# Revit family: Faucet-Brizo-Tresa-Single Handle Vessel Lavatory Faucet-65436LF
name_source: partatom
category: Plumbing Fixtures
units: mm (PartAtom-declared; Revit-internal decimal feet)

## family parameters
Always vertical = Yes
Cut with Voids When Loaded = No
OmniClass Number = 23.45.00.00
OmniClass Title = Sanitary, Laundry, and Cleaning Equipment
Part Type = Normal
Room Calculation Point = No
Round Connector Dimension = Use Radius
Shared = No
Work Plane-Based = Yes

## types (1)
- Polished Chrome
    Actual Valve Water Flow = 0
    Assembly Code = D2010400
    Connector Radius = 0' - 0 1/2"
    Default Elevation = 4' - 0"
    Description = Single Handle Vessel Lavatory Faucet
    Design Valve Water Flow = 0
    Finish = Steel-Brizo-Polished Chrome
    Flow = 2 GPM
    Height = 1' - 0 11/32"
    Makeup Water Flow = 0
    Manufacturer = Brizo
    Model = 65436LF-PC
    Product Documentation Link = https://media.brizo.com
    Product Name = Tresa® Collection
    Style = Lavatory Faucet
    Type Comments = Polished Chrome
    URL = http://www.brizo.com
    Vent Connection = No
    Waste Connection = No
    Width = 0' - 6 3/4"

## geometry (parser evidence)
native form markers: Blend x4, Sweep x2
no freeform markers — native parametric forms only
